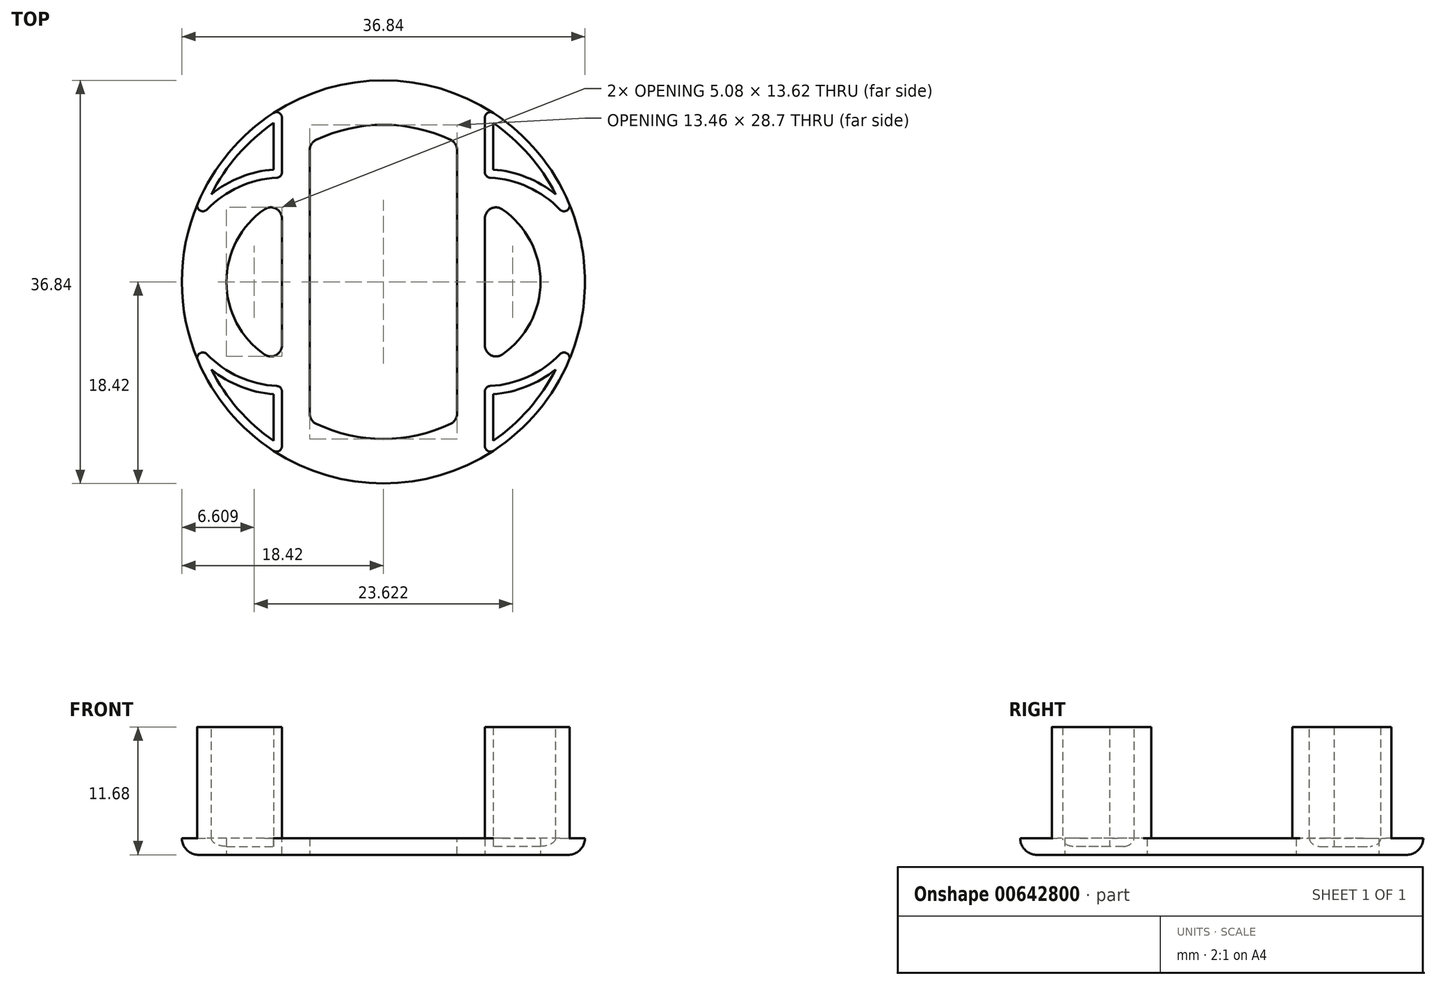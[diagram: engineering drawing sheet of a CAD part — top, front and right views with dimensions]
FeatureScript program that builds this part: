
annotation { "Feature Type Name" : "Feature", "Feature Type Description" : "" }
export const myFeature = defineFeature(function(context is Context, id is Id, definition is map)
    precondition{}
    {
        {
            var Q0;
            Q0=qCreatedBy(makeId("Top.planeOp"),FACE);
            var sketch = newSketch(context, id + "F0", { "sketchPlane" : qUnion([Q0])});
            skCircle(sketch, "E0", {"center": v(0, 0) * mm, "radius": 18.41 * mm});
            skSolve(sketch);
        }
        {
            var Q0;
            Q0=qSketchRegion(id+"F0",true);
            extrude(context, id + "F1", {"entities" : qUnion([Q0]), "depth" : 1.52 * mm, "offsetDistance" : 25.4 * mm});
        }
        {
            var Q0;
            Q0=makeQuery(id+"F1.opExtrude","CAP_FACE",FACE,{"disambiguationData":[OSD([sQuery(id+"F0.wireOp",EDGE,"E0")])],"isStart":false});
            var sketch = newSketch(context, id + "F2", { "sketchPlane" : qUnion([Q0])});
            skLineSegment(sketch, "E1.bottom", {"start": v(-9.27, 9.53) * mm, "end": v(9.27, 9.53) * mm, "construction": true});
            skLineSegment(sketch, "E1.top", {"start": v(-9.27, -9.53) * mm, "end": v(9.27, -9.53) * mm, "construction": true});
            skLineSegment(sketch, "E1.left", {"start": v(-9.27, 9.52) * mm, "end": v(-9.27, -9.53) * mm, "construction": true});
            skLineSegment(sketch, "E1.right", {"start": v(9.27, 9.53) * mm, "end": v(9.27, -9.53) * mm, "construction": true});
            skPoint(sketch, "E1.middle", {"position": v(0, 0) * mm});
            skArc(sketch, "E2", {"start": v(-9.27, 9.52) * mm, "mid": v(-14.52, 7.95) * mm, "end": v(-18.03, 3.74) * mm});
            skArc(sketch, "E3", {"start": v(9.27, -9.52) * mm, "mid": v(14.52, -7.95) * mm, "end": v(18.03, -3.74) * mm});
            skArc(sketch, "E4", {"start": v(-18.03, 3.74) * mm, "mid": v(-18.8, 0) * mm, "end": v(-18.03, -3.74) * mm, "construction": true});
            skArc(sketch, "E5", {"start": v(-18.03, 3.74) * mm, "mid": v(-18.41, 0) * mm, "end": v(-18.03, -3.74) * mm, "construction": true});
            skArc(sketch, "E6", {"start": v(-18.03, -3.74) * mm, "mid": v(0, -18.41) * mm, "end": v(18.03, -3.74) * mm});
            skArc(sketch, "E7", {"start": v(-18.03, -3.74) * mm, "mid": v(-14.52, -7.95) * mm, "end": v(-9.27, -9.53) * mm});
            skArc(sketch, "E8", {"start": v(18.03, 3.74) * mm, "mid": v(14.52, 7.95) * mm, "end": v(9.27, 9.53) * mm});
            skLineSegment(sketch, "E9", {"start": v(18.03, -3.74) * mm, "end": v(18.03, -3.74) * mm});
            skArc(sketch, "E10", {"start": v(18.03, -3.74) * mm, "mid": v(18.8, 0) * mm, "end": v(18.03, 3.74) * mm, "construction": true});
            skLineSegment(sketch, "E11", {"start": v(18.03, 3.74) * mm, "end": v(18.03, 3.74) * mm});
            skArc(sketch, "E12", {"start": v(18.03, 3.74) * mm, "mid": v(0, 18.41) * mm, "end": v(-18.03, 3.74) * mm});
            skArc(sketch, "E13", {"start": v(18.03, -3.74) * mm, "mid": v(18.41, 0) * mm, "end": v(18.03, 3.74) * mm, "construction": true});
            skLineSegment(sketch, "E14", {"start": v(-9.27, -9.53) * mm, "end": v(-9.27, -15.91) * mm});
            skLineSegment(sketch, "E15", {"start": v(9.27, -9.53) * mm, "end": v(9.27, -15.91) * mm});
            skLineSegment(sketch, "E16", {"start": v(9.27, 9.53) * mm, "end": v(9.27, 15.91) * mm});
            skLineSegment(sketch, "E17", {"start": v(-9.27, 9.53) * mm, "end": v(-9.27, 15.91) * mm});
            skArc(sketch, "E18", {"start": v(9.27, 15.91) * mm, "mid": v(0, 18.41) * mm, "end": v(-9.27, 15.91) * mm});
            skArc(sketch, "E19", {"start": v(-9.27, -15.91) * mm, "mid": v(0, -18.41) * mm, "end": v(9.27, -15.91) * mm});
            skSolve(sketch);
        }
        {
            var Q0;
            Q0=qSketchRegion(id+"F2",true);
            extrude(context, id + "F3", {"entities" : qUnion([Q0]), "operationType" : NewBodyOperationType.ADD, "depth" : 10.16 * mm, "offsetDistance" : 25.4 * mm});
        }
        {
            var Q0;
            Q0=makeQuery(id+"F1.opExtrude","CAP_EDGE",EDGE,{"disambiguationData":[OSD([sQuery(id+"F0.wireOp",EDGE,"E0")])],"isStart":true});
            fillet(context, id + "F4", {"entities" : qUnion([Q0]), "radius" : 1.52 * mm, "tangentPropagation" : true, "allowEdgeOverflow" : false});
        }
        {
            var Q0;
            Q0=makeQuery(id+"F3.opExtrude","SWEPT_EDGE",EDGE,{"disambiguationData":[OSD([sQuery(id+"F0.wireOp",EDGE,"E0"),sQuery(id+"F2.wireOp",EDGE,"E2"),sQuery(id+"F2.wireOp",EDGE,"E12")])]});
            var Q1;
            Q1=makeQuery(id+"F3.opExtrude","SWEPT_EDGE",EDGE,{"disambiguationData":[OSD([sQuery(id+"F0.wireOp",EDGE,"E0"),sQuery(id+"F2.wireOp",EDGE,"E6"),sQuery(id+"F2.wireOp",EDGE,"E7")])]});
            var Q2;
            Q2=makeQuery(id+"F3.opExtrude","SWEPT_EDGE",EDGE,{"disambiguationData":[OSD([sQuery(id+"F0.wireOp",EDGE,"E0"),sQuery(id+"F2.wireOp",EDGE,"E8"),sQuery(id+"F2.wireOp",EDGE,"E12")])]});
            var Q3;
            Q3=makeQuery(id+"F3.opExtrude","SWEPT_EDGE",EDGE,{"disambiguationData":[OSD([sQuery(id+"F0.wireOp",EDGE,"E0"),sQuery(id+"F2.wireOp",EDGE,"E3"),sQuery(id+"F2.wireOp",EDGE,"E6")])]});
            var Q4;
            Q4=makeQuery(id+"F3.opExtrude","SWEPT_EDGE",EDGE,{"disambiguationData":[OSD([sQuery(id+"F2.wireOp",EDGE,"E6"),sQuery(id+"F2.wireOp",EDGE,"E14"),sQuery(id+"F2.wireOp",EDGE,"E19")])]});
            var Q5;
            Q5=makeQuery(id+"F3.opExtrude","SWEPT_EDGE",EDGE,{"disambiguationData":[OSD([sQuery(id+"F0.wireOp",EDGE,"RRU1Pf1V-DoVO-Xhje-gmtz-4FpblWX3eckG.bottom"),sQuery(id+"F0.wireOp",EDGE,"RRU1Pf1V-DoVO-Xhje-gmtz-4FpblWX3eckG.left"),sQuery(id+"F2.wireOp",EDGE,"E7"),sQuery(id+"F2.wireOp",EDGE,"E14")])]});
            var Q6;
            Q6=makeQuery(id+"F3.opExtrude","SWEPT_EDGE",EDGE,{"disambiguationData":[OSD([sQuery(id+"F0.wireOp",EDGE,"RRU1Pf1V-DoVO-Xhje-gmtz-4FpblWX3eckG.top"),sQuery(id+"F0.wireOp",EDGE,"RRU1Pf1V-DoVO-Xhje-gmtz-4FpblWX3eckG.left"),sQuery(id+"F2.wireOp",EDGE,"E2"),sQuery(id+"F2.wireOp",EDGE,"E17")])]});
            var Q7;
            Q7=makeQuery(id+"F3.opExtrude","SWEPT_EDGE",EDGE,{"disambiguationData":[OSD([sQuery(id+"F2.wireOp",EDGE,"E12"),sQuery(id+"F2.wireOp",EDGE,"E17"),sQuery(id+"F2.wireOp",EDGE,"E18")])]});
            var Q8;
            Q8=makeQuery(id+"F3.opExtrude","SWEPT_EDGE",EDGE,{"disambiguationData":[OSD([sQuery(id+"F2.wireOp",EDGE,"E12"),sQuery(id+"F2.wireOp",EDGE,"E16"),sQuery(id+"F2.wireOp",EDGE,"E18")])]});
            var Q9;
            Q9=makeQuery(id+"F3.opExtrude","SWEPT_EDGE",EDGE,{"disambiguationData":[OSD([sQuery(id+"F2.wireOp",EDGE,"E6"),sQuery(id+"F2.wireOp",EDGE,"E15"),sQuery(id+"F2.wireOp",EDGE,"E19")])]});
            var Q10;
            Q10=makeQuery(id+"F3.opExtrude","SWEPT_EDGE",EDGE,{"disambiguationData":[OSD([sQuery(id+"F0.wireOp",EDGE,"RRU1Pf1V-DoVO-Xhje-gmtz-4FpblWX3eckG.top"),sQuery(id+"F0.wireOp",EDGE,"RRU1Pf1V-DoVO-Xhje-gmtz-4FpblWX3eckG.right"),sQuery(id+"F2.wireOp",EDGE,"E8"),sQuery(id+"F2.wireOp",EDGE,"E16")])]});
            var Q11;
            Q11=makeQuery(id+"F3.opExtrude","SWEPT_EDGE",EDGE,{"disambiguationData":[OSD([sQuery(id+"F0.wireOp",EDGE,"RRU1Pf1V-DoVO-Xhje-gmtz-4FpblWX3eckG.bottom"),sQuery(id+"F0.wireOp",EDGE,"RRU1Pf1V-DoVO-Xhje-gmtz-4FpblWX3eckG.right"),sQuery(id+"F2.wireOp",EDGE,"E3"),sQuery(id+"F2.wireOp",EDGE,"E15")])]});
            fillet(context, id + "F5", {"entities" : qUnion([Q0, Q1, Q2, Q3, Q4, Q5, Q6, Q7, Q8, Q9, Q10, Q11]), "radius" : 0.5 * mm, "tangentPropagation" : true, "allowEdgeOverflow" : false});
        }
        {
            var Q0;
            Q0=makeQuery(id+"F3.opExtrude","CAP_FACE",FACE,{"disambiguationData":[OSD([sQuery(id+"F2.wireOp",EDGE,"E1.bottom"),sQuery(id+"F2.wireOp",EDGE,"E2"),sQuery(id+"F2.wireOp",EDGE,"E8"),sQuery(id+"F2.wireOp",EDGE,"E12")])],"isStart":false});
            var Q1;
            Q1=makeQuery(id+"F3.opExtrude","CAP_FACE",FACE,{"disambiguationData":[OSD([sQuery(id+"F2.wireOp",EDGE,"E1.top"),sQuery(id+"F2.wireOp",EDGE,"E3"),sQuery(id+"F2.wireOp",EDGE,"E6"),sQuery(id+"F2.wireOp",EDGE,"E7")])],"isStart":false});
            shell(context, id + "F6", {"entities" : qUnion([Q0, Q1]), "thickness" : 0.76 * mm});
        }
        {
            var Q0;
            Q0=makeQuery(id+"F1.opExtrude","CAP_FACE",FACE,{"disambiguationData":[OSD([sQuery(id+"F0.wireOp",EDGE,"E0")])],"isStart":true});
            var sketch = newSketch(context, id + "F7", { "sketchPlane" : qUnion([Q0])});
            skLineSegment(sketch, "E20.bottom", {"start": v(6.73, -12.67) * mm, "end": v(-6.73, -12.67) * mm, "construction": true});
            skLineSegment(sketch, "E20.top", {"start": v(6.73, 12.67) * mm, "end": v(-6.73, 12.67) * mm, "construction": true});
            skLineSegment(sketch, "E20.left", {"start": v(6.73, -12.67) * mm, "end": v(6.73, 12.67) * mm});
            skLineSegment(sketch, "E20.right", {"start": v(-6.73, -12.67) * mm, "end": v(-6.73, 12.67) * mm});
            skPoint(sketch, "E20.middle", {"position": v(0, 0) * mm});
            skArc(sketch, "E21", {"start": v(-6.73, -12.67) * mm, "mid": v(0, -14.35) * mm, "end": v(6.73, -12.67) * mm});
            skArc(sketch, "E22", {"start": v(6.73, 12.67) * mm, "mid": v(0, 14.35) * mm, "end": v(-6.73, 12.67) * mm});
            skLineSegment(sketch, "E23", {"start": v(0, -14.35) * mm, "end": v(0, -16.9) * mm, "construction": true});
            skLineSegment(sketch, "E24", {"start": v(6.73, -12.67) * mm, "end": v(9.27, -12.67) * mm, "construction": true});
            skLineSegment(sketch, "E25", {"start": v(9.27, -7.48) * mm, "end": v(9.27, 7.48) * mm});
            skPoint(sketch, "E26", {"position": v(9.27, 0) * mm});
            skArc(sketch, "E27", {"start": v(9.27, -7.48) * mm, "mid": v(14.35, 0) * mm, "end": v(9.27, 7.48) * mm});
            skLineSegment(sketch, "E28", {"start": v(14.35, 0) * mm, "end": v(16.9, 0) * mm, "construction": true});
            skLineSegment(sketch, "E29", {"start": v(9.27, -7.48) * mm, "end": v(9.27, -10.02) * mm, "construction": true});
            skLineSegment(sketch, "E30", {"start": v(-9.27, -7.48) * mm, "end": v(-9.27, 7.48) * mm});
            skArc(sketch, "E31", {"start": v(-9.27, 7.48) * mm, "mid": v(-14.35, 0) * mm, "end": v(-9.27, -7.48) * mm});
            skLineSegment(sketch, "E32", {"start": v(-14.35, 0) * mm, "end": v(-16.9, 0) * mm, "construction": true});
            skSolve(sketch);
        }
        {
            var Q0;
            Q0 = qSketchRegion(id + "F7", true);
            var Q1;
            Q1=makeQuery(id+"F1.opExtrude","CAP_FACE",FACE,{"disambiguationData":[OSD([sQuery(id+"F0.wireOp",EDGE,"E0")])],"isStart":false});
            extrude(context, id + "F8", {"entities" : qUnion([Q0]), "operationType" : NewBodyOperationType.REMOVE, "endBound" : BoundingType.UP_TO_SURFACE, "oppositeDirection" : true, "depth" : 25.4 * mm, "endBoundEntityFace" : qUnion([Q1]), "offsetDistance" : 25.4 * mm});
        }
        {
            var Q0;
            Q0=makeQuery(id+"F3.opExtrude","CAP_EDGE",EDGE,{"disambiguationData":[OSD([sQuery(id+"F2.wireOp",EDGE,"E2")])],"isStart":true});
            var Q1;
            Q1=makeQuery(id+"F3.opExtrude","CAP_EDGE",EDGE,{"disambiguationData":[OSD([sQuery(id+"F2.wireOp",EDGE,"E7")])],"isStart":true});
            var Q2;
            Q2=makeQuery(id+"F3.opExtrude","CAP_EDGE",EDGE,{"disambiguationData":[OSD([sQuery(id+"F2.wireOp",EDGE,"E3")])],"isStart":true});
            var Q3;
            Q3=makeQuery(id+"F3.opExtrude","CAP_EDGE",EDGE,{"disambiguationData":[OSD([sQuery(id+"F2.wireOp",EDGE,"E8")])],"isStart":true});
            var Q4;
            {var subQ0=sQuery(id+"F7.wireOp",EDGE,"E31");var subQ1=sQuery(id+"F7.wireOp",EDGE,"E30");Q4=makeQuery(id+"F8.boolean.opBoolean","COPY",EDGE,{"derivedFrom":makeQuery(id+"F8.opExtrude","SWEPT_EDGE",EDGE,{"disambiguationData":[OSD([subQ1,subQ0]),TDD([makeQuery(id+"F7.imprint","INTERSECT",VERTEX,{"disambiguationData":[OD(0.0)],"derivedFrom":[subQ1,subQ0]})])]})});}
            var Q5;
            Q5=makeQuery(id+"F8.boolean.opBoolean","COPY",EDGE,{"derivedFrom":makeQuery(id+"F8.opExtrude","SWEPT_EDGE",EDGE,{"disambiguationData":[OSD([sQuery(id+"F7.wireOp",EDGE,"E20.right"),sQuery(id+"F7.wireOp",EDGE,"E21")])]})});
            var Q6;
            Q6=makeQuery(id+"F8.boolean.opBoolean","COPY",EDGE,{"derivedFrom":makeQuery(id+"F8.opExtrude","SWEPT_EDGE",EDGE,{"disambiguationData":[OSD([sQuery(id+"F7.wireOp",EDGE,"E20.left"),sQuery(id+"F7.wireOp",EDGE,"E21")])]})});
            var Q7;
            {var subQ0=sQuery(id+"F7.wireOp",EDGE,"E31");var subQ1=sQuery(id+"F7.wireOp",EDGE,"E30");Q7=makeQuery(id+"F8.boolean.opBoolean","COPY",EDGE,{"derivedFrom":makeQuery(id+"F8.opExtrude","SWEPT_EDGE",EDGE,{"disambiguationData":[OSD([subQ1,subQ0]),TDD([makeQuery(id+"F7.imprint","INTERSECT",VERTEX,{"disambiguationData":[OD(1.0)],"derivedFrom":[subQ1,subQ0]})])]})});}
            var Q8;
            Q8=makeQuery(id+"F8.boolean.opBoolean","COPY",EDGE,{"derivedFrom":makeQuery(id+"F8.opExtrude","SWEPT_EDGE",EDGE,{"disambiguationData":[OSD([sQuery(id+"F7.wireOp",EDGE,"E20.left"),sQuery(id+"F7.wireOp",EDGE,"E22")])]})});
            var Q9;
            {var subQ0=sQuery(id+"F7.wireOp",EDGE,"E27");var subQ1=sQuery(id+"F7.wireOp",EDGE,"E25");Q9=makeQuery(id+"F8.boolean.opBoolean","COPY",EDGE,{"derivedFrom":makeQuery(id+"F8.opExtrude","SWEPT_EDGE",EDGE,{"disambiguationData":[OSD([subQ1,subQ0]),TDD([makeQuery(id+"F7.imprint","INTERSECT",VERTEX,{"disambiguationData":[OD(1.0)],"derivedFrom":[subQ1,subQ0]})])]})});}
            var Q10;
            Q10=makeQuery(id+"F8.boolean.opBoolean","COPY",EDGE,{"derivedFrom":makeQuery(id+"F8.opExtrude","SWEPT_EDGE",EDGE,{"disambiguationData":[OSD([sQuery(id+"F7.wireOp",EDGE,"E20.right"),sQuery(id+"F7.wireOp",EDGE,"E22")])]})});
            var Q11;
            {var subQ0=sQuery(id+"F7.wireOp",EDGE,"E27");var subQ1=sQuery(id+"F7.wireOp",EDGE,"E25");Q11=makeQuery(id+"F8.boolean.opBoolean","COPY",EDGE,{"derivedFrom":makeQuery(id+"F8.opExtrude","SWEPT_EDGE",EDGE,{"disambiguationData":[OSD([subQ1,subQ0]),TDD([makeQuery(id+"F7.imprint","INTERSECT",VERTEX,{"disambiguationData":[OD(0.0)],"derivedFrom":[subQ1,subQ0]})])]})});}
            fillet(context, id + "F9", {"entities" : qUnion([Q0, Q1, Q2, Q3, Q4, Q5, Q6, Q7, Q8, Q9, Q10, Q11]), "radius" : 1.02 * mm, "tangentPropagation" : true, "allowEdgeOverflow" : false});
        }
    });
